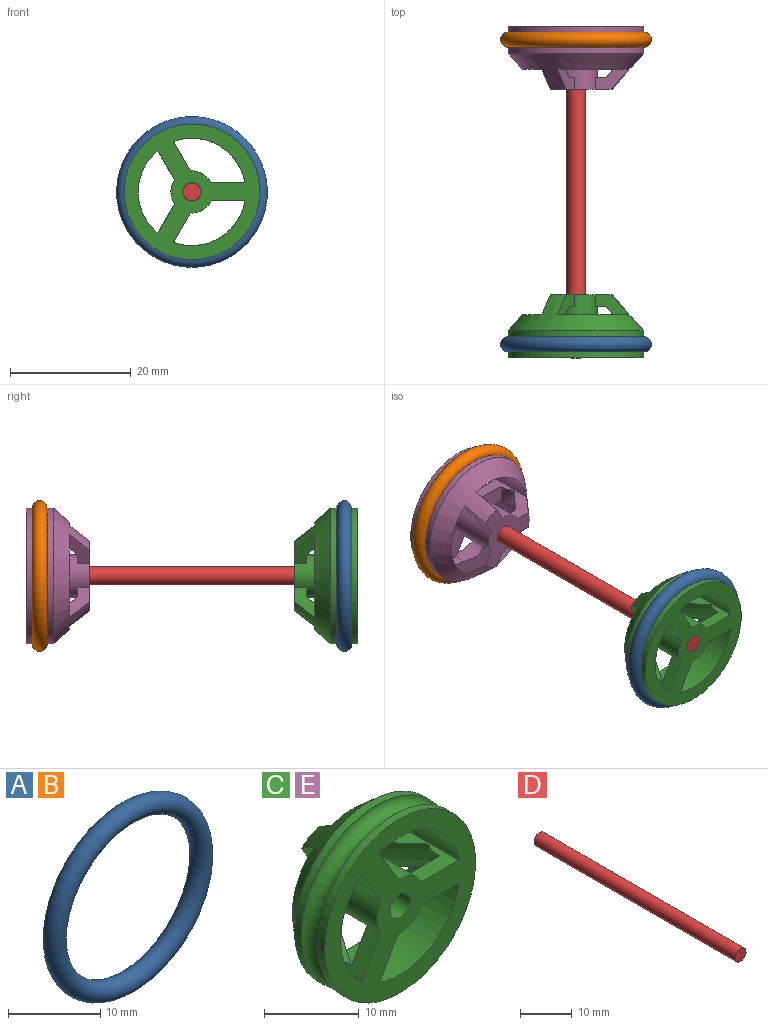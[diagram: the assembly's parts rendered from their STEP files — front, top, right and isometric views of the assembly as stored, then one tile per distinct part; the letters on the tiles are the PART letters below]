
ASSEMBLY  parts=5 mates=3
PART A: 1 faces, bbox 27.1x2.5x27.1 mm
  f0: torus R=11.25mm, axis (0,-1,0), area 555.2mm2
PART B: same geometry as A
PART C: 29 faces, bbox 26.5x10.8x26.5 mm
  f0: torus R=11.25mm, axis (0,1,0), area 7.5mm2, adj f5,f17,f18,f19
  f1: torus R=11.25mm, axis (0,1,0), area 7.5mm2, adj f6,f23,f24,f25
  f2: torus R=11.25mm, axis (0,1,0), area 7.5mm2, adj f7,f20,f21,f22
  f3: plane 11.56x10.2mm, normal (0,1,0), area 54.3mm2, adj f4,f15,f16,f17,f18,f20,f21,f23
  f4: cone r=11.25mm half-angle=41.2deg, axis (0,-1,0), area 266.6mm2, adj f3,f12,f17,f18,f20,f21,f23,f24
  f5: cone r=9.74mm half-angle=41.2deg, axis (0,-1,0), area 17.7mm2, adj f0,f8,f17,f18
  f6: cone r=9.74mm half-angle=41.2deg, axis (0,-1,0), area 17.7mm2, adj f1,f9,f23,f24
  f7: cone r=9.74mm half-angle=41.2deg, axis (0,-1,0), area 17.7mm2, adj f2,f10,f20,f21
  f8: plane 3x1.93mm, normal (0,-1,0), area 4.9mm2, adj f5,f16,f17,f18
  f9: plane 3.45x2.98mm, normal (0,-1,0), area 4.9mm2, adj f6,f16,f23,f24
  f10: plane 3.45x2.98mm, normal (0,-1,0), area 4.9mm2, adj f7,f16,f20,f21
  f11: plane 22.5x22.5mm, normal (0,-1,0), area 229.2mm2, adj f14,f15,f16,f17,f18,f20,f21,f23
  f12: cylinder r=11.25mm len=22.5mm, axis (0,1,0), area 70.7mm2, adj f4,f13
  f13: torus R=11.25mm, axis (0,1,0), area 257.9mm2, adj f12,f14
  f14: cylinder r=11.25mm len=22.5mm, axis (0,1,0), area 70.7mm2, adj f11,f13
  f15: cylinder r=1.5mm len=10.5mm, axis (0,-1,0), area 99mm2, adj f3,f11
  f16: cylinder r=3.5mm len=10.5mm, axis (0,-1,0), area 193.7mm2, adj f3,f8,f9,f10,f11,f17,f18,f19
  f17: plane 10.74x5.85mm, normal (0,0,1), area 27.6mm2, adj f0,f3,f4,f5,f8,f11,f16,f19
  f18: plane 10.74x5.85mm, normal (0,0,-1), area 27.6mm2, adj f0,f3,f4,f5,f8,f11,f16,f19
  f19: plane 4.85x3mm, normal (0,1,0), area 13.7mm2, adj f0,f16,f17,f18
  f20: plane 10.74x5.1mm, normal (-0.87,0,-0.5), area 27.6mm2, adj f2,f3,f4,f7,f10,f11,f16,f22
  f21: plane 10.74x5.1mm, normal (0.87,0,0.5), area 27.6mm2, adj f2,f3,f4,f7,f10,f11,f16,f22
  f22: plane 5.58x4.95mm, normal (0,1,0), area 13.7mm2, adj f2,f16,f20,f21
  f23: plane 10.74x5.1mm, normal (0.87,0,-0.5), area 27.6mm2, adj f1,f3,f4,f6,f9,f11,f16,f25
  f24: plane 10.74x5.1mm, normal (-0.87,0,0.5), area 27.6mm2, adj f1,f3,f4,f6,f9,f11,f16,f25
  f25: plane 5.58x4.95mm, normal (0,1,0), area 13.7mm2, adj f1,f16,f23,f24
  f26: cylinder r=8.9mm len=11.87mm, axis (0,-1,0), area 112.3mm2, adj f4,f11,f17,f21
  f27: cylinder r=8.9mm len=13.7mm, axis (0,-1,0), area 112.3mm2, adj f4,f11,f20,f24
  f28: cylinder r=8.9mm len=11.87mm, axis (0,-1,0), area 112.3mm2, adj f4,f11,f18,f23
PART D: 3 faces, bbox 3x55x3 mm
  f0: plane 3x3mm, normal (0,-1,0), area 7.1mm2, adj f2
  f1: plane 3x3mm, normal (0,1,0), area 7.1mm2, adj f2
  f2: cylinder r=1.5mm len=55mm, axis (0,1,0), area 518.4mm2, adj f0,f1
PART E: same geometry as C
PLACE A t=(20,80.5,25)mm
PLACE B t=(20,131,25)mm
PLACE C t=(-6.58,9.27,-3.9)mm
PLACE D at identity
PLACE E rot(axis=(1,0,0),180deg) t=(-6.58,5.73,88.9)mm
MATE fastened E.f0 <-> D.f2  axis (0,1,0) through (-142.5,35,42.5)mm
MATE fastened A.f0 <-> C.f0  axis (0,-1,0) through (-142.5,-17.75,42.5)mm
MATE fastened B.f0 <-> E.f0  axis (0,-1,0) through (-142.5,32.75,42.5)mm
